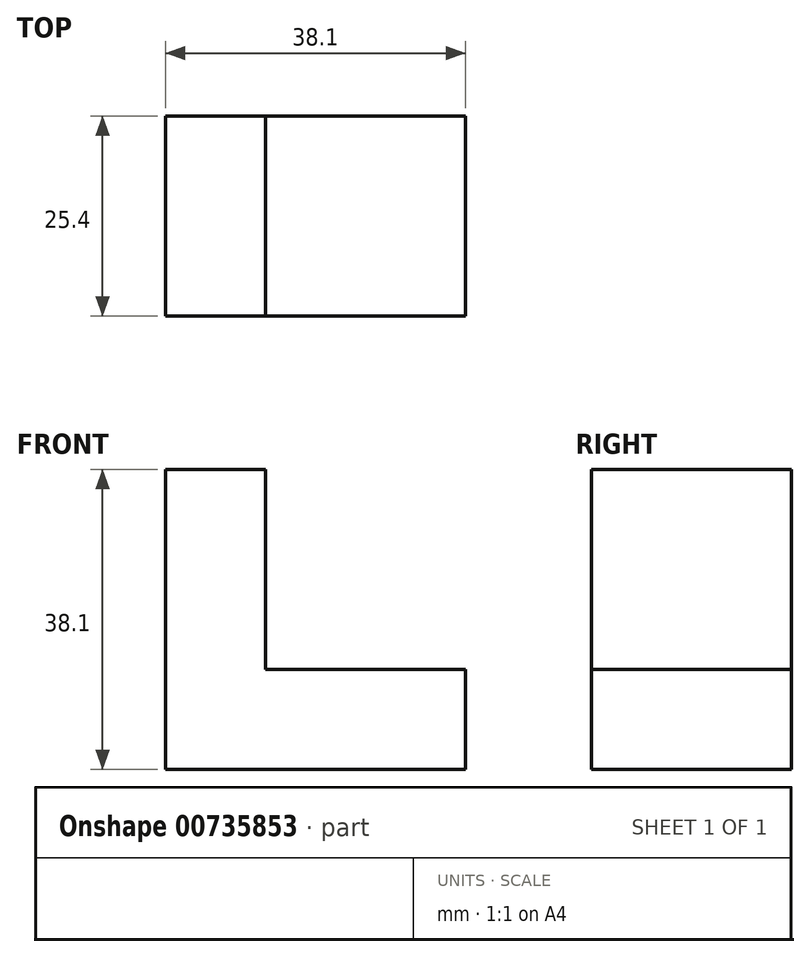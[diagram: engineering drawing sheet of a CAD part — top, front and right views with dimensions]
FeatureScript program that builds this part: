
annotation { "Feature Type Name" : "Feature", "Feature Type Description" : "" }
export const myFeature = defineFeature(function(context is Context, id is Id, definition is map)
    precondition{}
    {
        {
            var Q0;
            Q0=qCreatedBy(makeId("Front.planeOp"),FACE);
            var sketch = newSketch(context, id + "F0", { "sketchPlane" : qUnion([Q0])});
            skLineSegment(sketch, "E0", {"start": v(0, 0) * mm, "end": v(38.1, 0) * mm});
            skLineSegment(sketch, "E1", {"start": v(38.1, 0) * mm, "end": v(38.1, 12.7) * mm});
            skLineSegment(sketch, "E2", {"start": v(38.1, 12.7) * mm, "end": v(12.7, 12.7) * mm});
            skLineSegment(sketch, "E3", {"start": v(12.7, 12.7) * mm, "end": v(12.7, 38.1) * mm});
            skLineSegment(sketch, "E4", {"start": v(12.7, 38.1) * mm, "end": v(0, 38.1) * mm});
            skLineSegment(sketch, "E5", {"start": v(0, 38.1) * mm, "end": v(0, 0) * mm});
            skLineSegment(sketch, "E6", {"start": v(12.7, 12.7) * mm, "end": v(38.1, 12.7) * mm});
            skSolve(sketch);
        }
        {
            var Q0;
            Q0=makeQuery(id+"F0.imprint","IMPRINT",FACE,{"disambiguationData":[TD([[makeQuery(id+"F0.imprint","IMPRINT",EDGE,{"derivedFrom":sQuery(id+"F0.wireOp",EDGE,"E0")}),1.0]])]});
            extrude(context, id + "F1", {"entities" : qUnion([Q0]), "depth" : 25.4 * mm, "offsetDistance" : 25.4 * mm});
        }
    });
